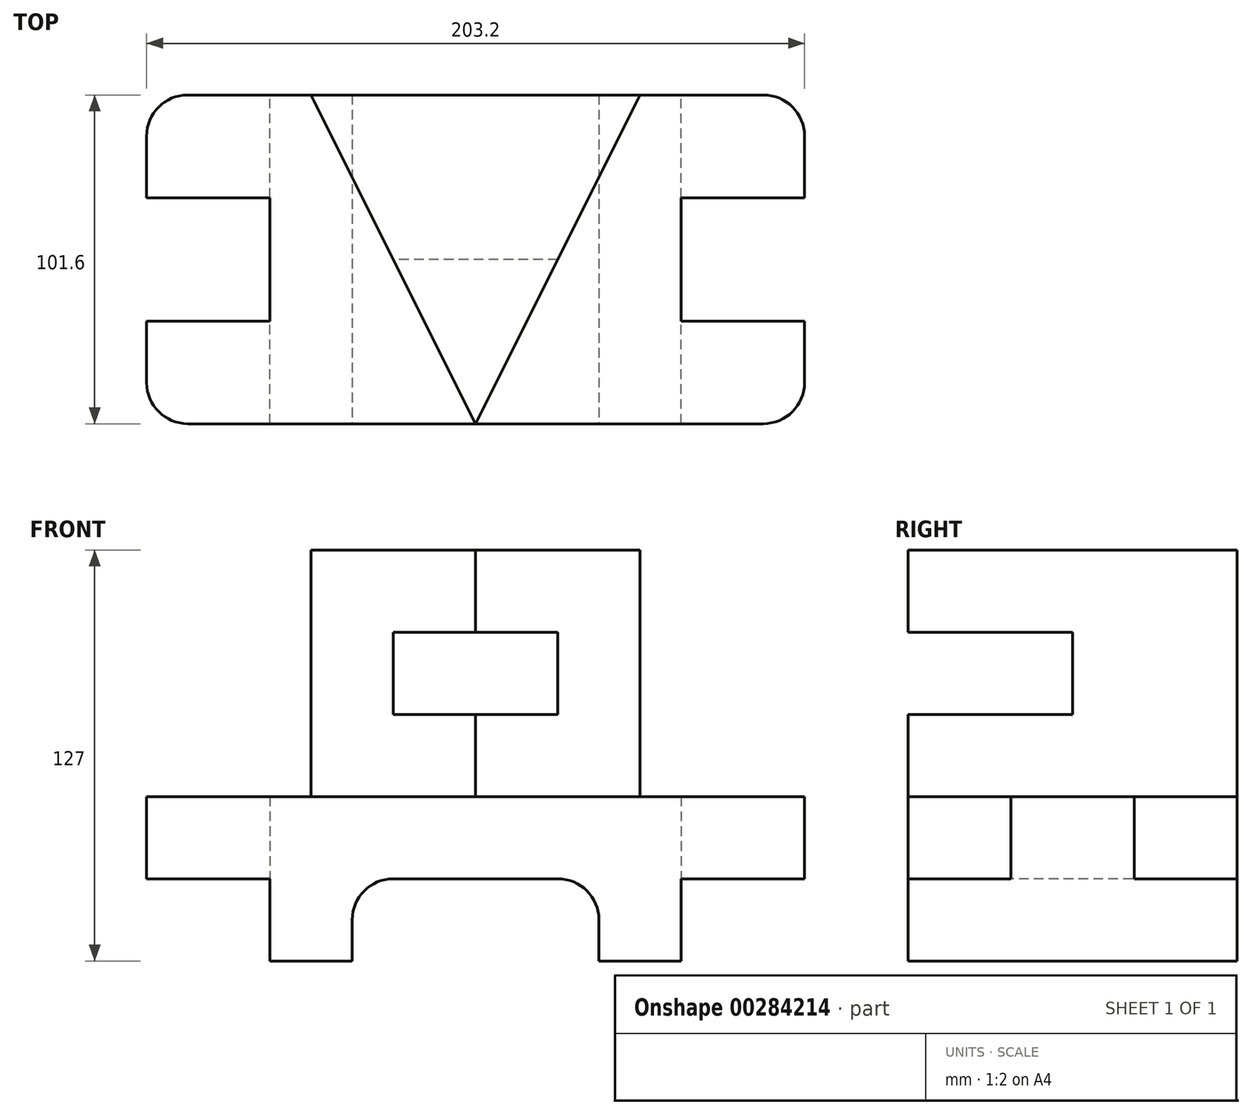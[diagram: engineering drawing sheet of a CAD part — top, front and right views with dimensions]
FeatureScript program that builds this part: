
annotation { "Feature Type Name" : "Feature", "Feature Type Description" : "" }
export const myFeature = defineFeature(function(context is Context, id is Id, definition is map)
    precondition{}
    {
        {
            var Q0;
            Q0=qCreatedBy(makeId("Front.planeOp"),FACE);
            var sketch = newSketch(context, id + "F0", { "sketchPlane" : qUnion([Q0])});
            skLineSegment(sketch, "E0", {"start": v(0, 0) * mm, "end": v(0, 25.4) * mm});
            skLineSegment(sketch, "E1", {"start": v(0, 25.4) * mm, "end": v(-38.1, 25.4) * mm});
            skLineSegment(sketch, "E2", {"start": v(-38.1, 25.4) * mm, "end": v(-38.1, 50.8) * mm});
            skLineSegment(sketch, "E3", {"start": v(-38.1, 50.8) * mm, "end": v(165.1, 50.8) * mm});
            skLineSegment(sketch, "E4", {"start": v(165.1, 50.8) * mm, "end": v(165.1, 25.4) * mm});
            skLineSegment(sketch, "E5", {"start": v(165.1, 25.4) * mm, "end": v(127, 25.4) * mm});
            skLineSegment(sketch, "E6", {"start": v(127, 25.4) * mm, "end": v(127, 0) * mm});
            skLineSegment(sketch, "E7", {"start": v(127, 0) * mm, "end": v(0, 0) * mm});
            skSolve(sketch);
        }
        {
            var Q0;
            Q0=makeQuery(id+"F0.imprint","IMPRINT",FACE,{"disambiguationData":[TD([[makeQuery(id+"F0.imprint","IMPRINT",EDGE,{"derivedFrom":sQuery(id+"F0.wireOp",EDGE,"E0")}),-1.0]])]});
            extrude(context, id + "F1", {"entities" : qUnion([Q0]), "endBound" : BoundingType.SYMMETRIC, "depth" : 101.6 * mm});
        }
        {
            var Q0;
            Q0=makeQuery(id+"F1.opExtrude","CAP_FACE",FACE,{"disambiguationData":[OSD([sQuery(id+"F0.wireOp",EDGE,"E0"),sQuery(id+"F0.wireOp",EDGE,"E1"),sQuery(id+"F0.wireOp",EDGE,"E2"),sQuery(id+"F0.wireOp",EDGE,"E3"),sQuery(id+"F0.wireOp",EDGE,"E4"),sQuery(id+"F0.wireOp",EDGE,"E5"),sQuery(id+"F0.wireOp",EDGE,"E6"),sQuery(id+"F0.wireOp",EDGE,"E7")])],"isStart":false});
            var sketch = newSketch(context, id + "F2", { "sketchPlane" : qUnion([Q0])});
            skLineSegment(sketch, "E8.bottom", {"start": v(25.4, 0) * mm, "end": v(101.6, 0) * mm});
            skLineSegment(sketch, "E8.top", {"start": v(25.4, 25.4) * mm, "end": v(101.6, 25.4) * mm});
            skLineSegment(sketch, "E8.left", {"start": v(25.4, 0) * mm, "end": v(25.4, 25.4) * mm});
            skLineSegment(sketch, "E8.right", {"start": v(101.6, 0) * mm, "end": v(101.6, 25.4) * mm});
            skSolve(sketch);
        }
        {
            var Q0;
            Q0=makeQuery(id+"F2.imprint","IMPRINT",FACE,{"disambiguationData":[TD([[makeQuery(id+"F2.imprint","IMPRINT",EDGE,{"derivedFrom":sQuery(id+"F2.wireOp",EDGE,"E8.bottom")}),-1.0]])]});
            extrude(context, id + "F3", {"entities" : qUnion([Q0]), "operationType" : NewBodyOperationType.REMOVE, "endBound" : BoundingType.THROUGH_ALL, "oppositeDirection" : true, "depth" : 25.4 * mm});
        }
        {
            var Q0;
            Q0=makeQuery(id+"F3.boolean.opBoolean","COPY",EDGE,{"derivedFrom":makeQuery(id+"F3.opExtrude","SWEPT_EDGE",EDGE,{"disambiguationData":[OSD([sQuery(id+"F2.wireOp",EDGE,"E8.top"),sQuery(id+"F2.wireOp",EDGE,"E8.left")])]})});
            fillet(context, id + "F4", {"entities" : qUnion([Q0]), "radius" : 12.7 * mm, "tangentPropagation" : true, "allowEdgeOverflow" : false});
        }
        {
            var Q0;
            Q0=makeQuery(id+"F3.boolean.opBoolean","COPY",EDGE,{"derivedFrom":makeQuery(id+"F3.opExtrude","SWEPT_EDGE",EDGE,{"disambiguationData":[OSD([sQuery(id+"F2.wireOp",EDGE,"E8.top"),sQuery(id+"F2.wireOp",EDGE,"E8.right")])]})});
            fillet(context, id + "F5", {"entities" : qUnion([Q0]), "radius" : 12.7 * mm, "tangentPropagation" : true, "allowEdgeOverflow" : false});
        }
        {
            var Q0;
            Q0=makeQuery(id+"F1.opExtrude","SWEPT_FACE",FACE,{"disambiguationData":[OSD([sQuery(id+"F0.wireOp",EDGE,"E4")])]});
            var sketch = newSketch(context, id + "F6", { "sketchPlane" : qUnion([Q0])});
            skLineSegment(sketch, "E9.bottom", {"start": v(-19.05, 50.8) * mm, "end": v(19.05, 50.8) * mm});
            skLineSegment(sketch, "E9.top", {"start": v(-19.05, 25.4) * mm, "end": v(19.05, 25.4) * mm});
            skLineSegment(sketch, "E9.left", {"start": v(-19.05, 50.8) * mm, "end": v(-19.05, 25.4) * mm});
            skLineSegment(sketch, "E9.right", {"start": v(19.05, 50.8) * mm, "end": v(19.05, 25.4) * mm});
            skSolve(sketch);
        }
        {
            var Q0;
            Q0=makeQuery(id+"F6.imprint","IMPRINT",FACE,{"disambiguationData":[TD([[makeQuery(id+"F6.imprint","IMPRINT",EDGE,{"derivedFrom":sQuery(id+"F6.wireOp",EDGE,"E9.bottom")}),-1.0]])]});
            extrude(context, id + "F7", {"entities" : qUnion([Q0]), "operationType" : NewBodyOperationType.REMOVE, "oppositeDirection" : true, "depth" : 38.1 * mm});
        }
        {
            var Q0;
            Q0=makeQuery(id+"F1.opExtrude","SWEPT_FACE",FACE,{"disambiguationData":[OSD([sQuery(id+"F0.wireOp",EDGE,"E2")])]});
            var sketch = newSketch(context, id + "F8", { "sketchPlane" : qUnion([Q0])});
            skLineSegment(sketch, "E10.bottom", {"start": v(-19.05, 50.8) * mm, "end": v(19.05, 50.8) * mm});
            skLineSegment(sketch, "E10.top", {"start": v(-19.05, 25.4) * mm, "end": v(19.05, 25.4) * mm});
            skLineSegment(sketch, "E10.left", {"start": v(-19.05, 50.8) * mm, "end": v(-19.05, 25.4) * mm});
            skLineSegment(sketch, "E10.right", {"start": v(19.05, 50.8) * mm, "end": v(19.05, 25.4) * mm});
            skSolve(sketch);
        }
        {
            var Q0;
            Q0=makeQuery(id+"F8.imprint","IMPRINT",FACE,{"disambiguationData":[TD([[makeQuery(id+"F8.imprint","IMPRINT",EDGE,{"derivedFrom":sQuery(id+"F8.wireOp",EDGE,"E10.bottom")}),1.0]])]});
            extrude(context, id + "F9", {"entities" : qUnion([Q0]), "operationType" : NewBodyOperationType.REMOVE, "oppositeDirection" : true, "depth" : 38.1 * mm});
        }
        {
            var Q0;
            Q0=makeQuery(id+"F1.opExtrude","CAP_EDGE",EDGE,{"disambiguationData":[OSD([sQuery(id+"F0.wireOp",EDGE,"E2")])],"isStart":false});
            var Q1;
            Q1=makeQuery(id+"F1.opExtrude","CAP_EDGE",EDGE,{"disambiguationData":[OSD([sQuery(id+"F0.wireOp",EDGE,"E2")])],"isStart":true});
            var Q2;
            Q2=makeQuery(id+"F1.opExtrude","CAP_EDGE",EDGE,{"disambiguationData":[OSD([sQuery(id+"F0.wireOp",EDGE,"E4")])],"isStart":true});
            var Q3;
            Q3=makeQuery(id+"F1.opExtrude","CAP_EDGE",EDGE,{"disambiguationData":[OSD([sQuery(id+"F0.wireOp",EDGE,"E4")])],"isStart":false});
            fillet(context, id + "F10", {"entities" : qUnion([Q0, Q1, Q2, Q3]), "radius" : 12.7 * mm, "tangentPropagation" : true, "allowEdgeOverflow" : false});
        }
        {
            var Q0;
            Q0=qCreatedBy(makeId("Front.planeOp"),FACE);
            var sketch = newSketch(context, id + "F11", { "sketchPlane" : qUnion([Q0])});
            skLineSegment(sketch, "E11.bottom", {"start": v(12.7, 50.8) * mm, "end": v(114.3, 50.8) * mm});
            skLineSegment(sketch, "E11.top", {"start": v(12.7, 127) * mm, "end": v(114.3, 127) * mm});
            skLineSegment(sketch, "E11.left", {"start": v(12.7, 50.8) * mm, "end": v(12.7, 127) * mm});
            skLineSegment(sketch, "E11.right", {"start": v(114.3, 50.8) * mm, "end": v(114.3, 127) * mm});
            skSolve(sketch);
        }
        {
            var Q0;
            Q0=makeQuery(id+"F11.imprint","IMPRINT",FACE,{"disambiguationData":[TD([[makeQuery(id+"F11.imprint","IMPRINT",EDGE,{"derivedFrom":sQuery(id+"F11.wireOp",EDGE,"E11.bottom")}),1.0]])]});
            extrude(context, id + "F12", {"entities" : qUnion([Q0]), "operationType" : NewBodyOperationType.ADD, "oppositeDirection" : true, "depth" : 50.8 * mm, "hasSecondDirection" : true, "secondDirectionOppositeDirection" : false, "secondDirectionDepth" : 50.8 * mm});
        }
        {
            var Q0;
            Q0=makeQuery(id+"F12.opExtrude","SWEPT_FACE",FACE,{"disambiguationData":[OSD([sQuery(id+"F11.wireOp",EDGE,"E11.top")])]});
            var sketch = newSketch(context, id + "F13", { "sketchPlane" : qUnion([Q0])});
            skLineSegment(sketch, "E12", {"start": v(12.7, 50.8) * mm, "end": v(63.5, -50.8) * mm});
            skLineSegment(sketch, "E13", {"start": v(63.5, -50.8) * mm, "end": v(114.3, 50.8) * mm});
            skLineSegment(sketch, "E14", {"start": v(114.3, 50.8) * mm, "end": v(12.7, 50.8) * mm});
            skSolve(sketch);
        }
        {
            var Q0;
            {var subQ0=sQuery(id+"F13.wireOp",EDGE,"E12");Q0=makeQuery(id+"F13.imprint","IMPRINT",FACE,{"disambiguationData":[TD([[makeQuery(id+"F13.imprint","IMPRINT",EDGE,{"derivedFrom":subQ0}),-1.0]])]});}
            var Q1;
            {var subQ0=sQuery(id+"F13.wireOp",EDGE,"E13");Q1=makeQuery(id+"F13.imprint","IMPRINT",FACE,{"disambiguationData":[TD([[makeQuery(id+"F13.imprint","IMPRINT",EDGE,{"derivedFrom":subQ0}),-1.0]])]});}
            extrude(context, id + "F14", {"entities" : qUnion([Q0, Q1]), "operationType" : NewBodyOperationType.REMOVE, "oppositeDirection" : true, "depth" : 76.2 * mm});
        }
        {
            var Q0;
            Q0=makeQuery(id+"F12.boolean.opBoolean","MERGE",FACE,{"derivedFrom":[makeQuery(id+"F1.opExtrude","CAP_FACE",FACE,{"disambiguationData":[OSD([sQuery(id+"F0.wireOp",EDGE,"E0"),sQuery(id+"F0.wireOp",EDGE,"E1"),sQuery(id+"F0.wireOp",EDGE,"E2"),sQuery(id+"F0.wireOp",EDGE,"E3"),sQuery(id+"F0.wireOp",EDGE,"E4"),sQuery(id+"F0.wireOp",EDGE,"E5"),sQuery(id+"F0.wireOp",EDGE,"E6"),sQuery(id+"F0.wireOp",EDGE,"E7")])],"isStart":true}),makeQuery(id+"F12.opExtrude","CAP_FACE",FACE,{"disambiguationData":[OSD([sQuery(id+"F11.wireOp",EDGE,"E11.bottom"),sQuery(id+"F11.wireOp",EDGE,"E11.top"),sQuery(id+"F11.wireOp",EDGE,"E11.left"),sQuery(id+"F11.wireOp",EDGE,"E11.right")])],"isStart":false})]});
            var sketch = newSketch(context, id + "F15", { "sketchPlane" : qUnion([Q0])});
            skLineSegment(sketch, "E15.bottom", {"start": v(-88.9, 101.6) * mm, "end": v(-38.1, 101.6) * mm});
            skLineSegment(sketch, "E15.top", {"start": v(-88.9, 76.2) * mm, "end": v(-38.1, 76.2) * mm});
            skLineSegment(sketch, "E15.left", {"start": v(-88.9, 101.6) * mm, "end": v(-88.9, 76.2) * mm});
            skLineSegment(sketch, "E15.right", {"start": v(-38.1, 101.6) * mm, "end": v(-38.1, 76.2) * mm});
            skSolve(sketch);
        }
        {
            var Q0;
            Q0=makeQuery(id+"F15.imprint","IMPRINT",FACE,{"disambiguationData":[TD([[makeQuery(id+"F15.imprint","IMPRINT",EDGE,{"derivedFrom":sQuery(id+"F15.wireOp",EDGE,"E15.bottom")}),-1.0]])]});
            extrude(context, id + "F16", {"entities" : qUnion([Q0]), "operationType" : NewBodyOperationType.REMOVE, "endBound" : BoundingType.THROUGH_ALL, "oppositeDirection" : true, "depth" : 25.4 * mm, "hasSecondDirection" : true, "secondDirectionBound" : SecondDirectionBoundingType.THROUGH_ALL, "secondDirectionOppositeDirection" : false, "secondDirectionDepth" : 25.4 * mm});
        }
        {
            var Q0;
            Q0=makeQuery(id+"F16.boolean.opBoolean","COPY",FACE,{"derivedFrom":makeQuery(id+"F16.opExtrude","SWEPT_FACE",FACE,{"disambiguationData":[OSD([sQuery(id+"F15.wireOp",EDGE,"E15.right")])]})});
            extrude(context, id + "F17", {"entities" : qUnion([Q0]), "operationType" : NewBodyOperationType.ADD, "depth" : 50.8 * mm});
        }
    });
